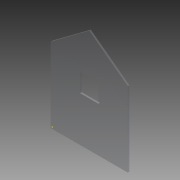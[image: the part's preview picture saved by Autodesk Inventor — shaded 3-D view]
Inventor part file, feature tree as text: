
AUTODESK INVENTOR PART (.ipt)
format: ipt  version: 2015 (Build 190159000, 159)  size: 118,272 bytes
history: native  units: in
note: dims shown in document units (in); Inventor stores cm internally (conversion verified against a paired STEP export)
features: sketch x5, extrude x4
ambient origin geometry x8: Origin, YZ Plane, XZ Plane, XY Plane, X Axis, Y Axis, Z Axis, Center Point
bodies: Solid1 (feature_tree)
feature tree (9):
  sketch  "Sketch1"  dims[d0=13.189in d1=17.7165in]
  extrude  "Extrusion1"  Depth=17.7165in
  extrude  "Extrusion2"  Depth=0.2756in TaperAngle=0.0deg
  extrude  "Extrusion3"  Depth=12.7953in
  extrude  "Extrusion5"  Depth=12.7953in
  sketch  "Sketch2"  dims[d2=6.5945in d3=0.2756in d4=0.0in]
  sketch  "Sketch3"  dims[d5=6.5945in d6=12.7953in]
  sketch  "Sketch5"  dims[d7=6.5369in d8=0.0in d10=12.7953in]
  sketch  "Sketch9"  dims[d11=12.0256in d12=0.0in d20=1.9685in d21=1.5748in d22=3.1496in d23=3.1496in d24=3.1496in d25=0.3937in d26=0.0in]
